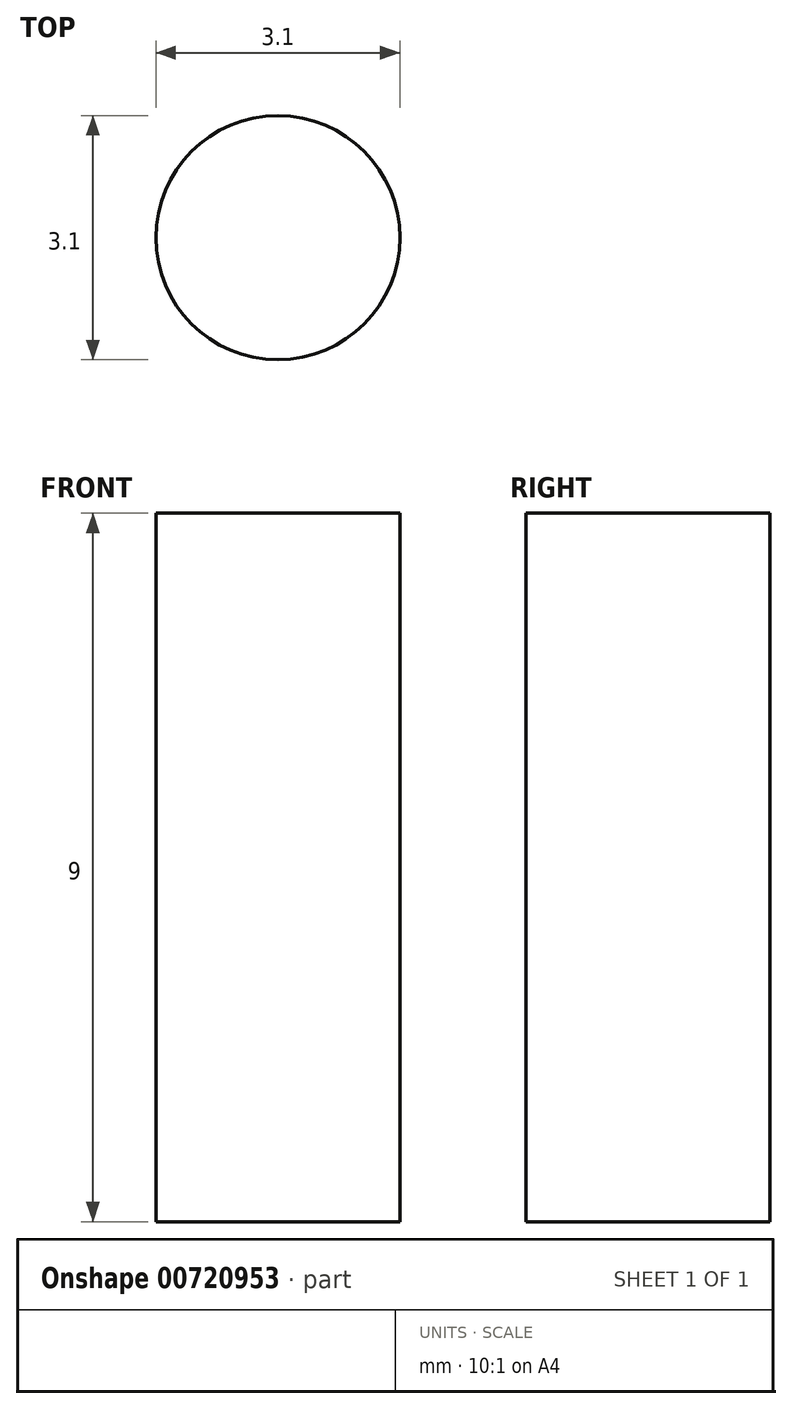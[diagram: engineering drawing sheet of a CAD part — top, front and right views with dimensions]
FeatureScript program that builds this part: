
annotation { "Feature Type Name" : "Feature", "Feature Type Description" : "" }
export const myFeature = defineFeature(function(context is Context, id is Id, definition is map)
    precondition{}
    {
        {
            var Q0;
            Q0=qCreatedBy(makeId("Top.planeOp"),FACE);
            var sketch = newSketch(context, id + "F0", { "sketchPlane" : qUnion([Q0])});
            skCircle(sketch, "E0", {"center": v(0, 0) * mm, "radius": 1.55 * mm});
            skSolve(sketch);
        }
        {
            var Q0;
            Q0 = qSketchRegion(id + "F0", true);
            extrude(context, id + "F1", {"entities" : qUnion([Q0]), "depth" : 9 * mm, "offsetDistance" : 25 * mm});
        }
    });
